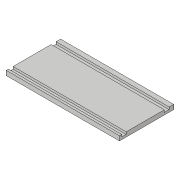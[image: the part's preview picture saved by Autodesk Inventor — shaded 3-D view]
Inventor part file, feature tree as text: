
AUTODESK INVENTOR PART (.ipt)
format: ipt  version: 2018.3 (Build 223284000, 284)  size: 93,184 bytes
history: native  units: in
note: dims shown in document units (in); Inventor stores cm internally (conversion verified against a paired STEP export)
features: extrude x2, sketch x2
ambient origin geometry x8: Origin, YZ Plane, XZ Plane, XY Plane, X Axis, Y Axis, Z Axis, Center Point
bodies: Solid1 (feature_tree)
feature tree (4):
  extrude  "Extrusion1"  Depth=1.5in
  extrude  "Extrusion2"  Depth=0.126in
  sketch  "Sketch1"  dims[d0=3.125in d1=1.5in]
  sketch  "Sketch2"  dims[d2=0.125in d3=0.0in d4=0.126in d6=0.0625in d7=0.0in d8=0.0625in d13=0.125in d14=0.135in]
